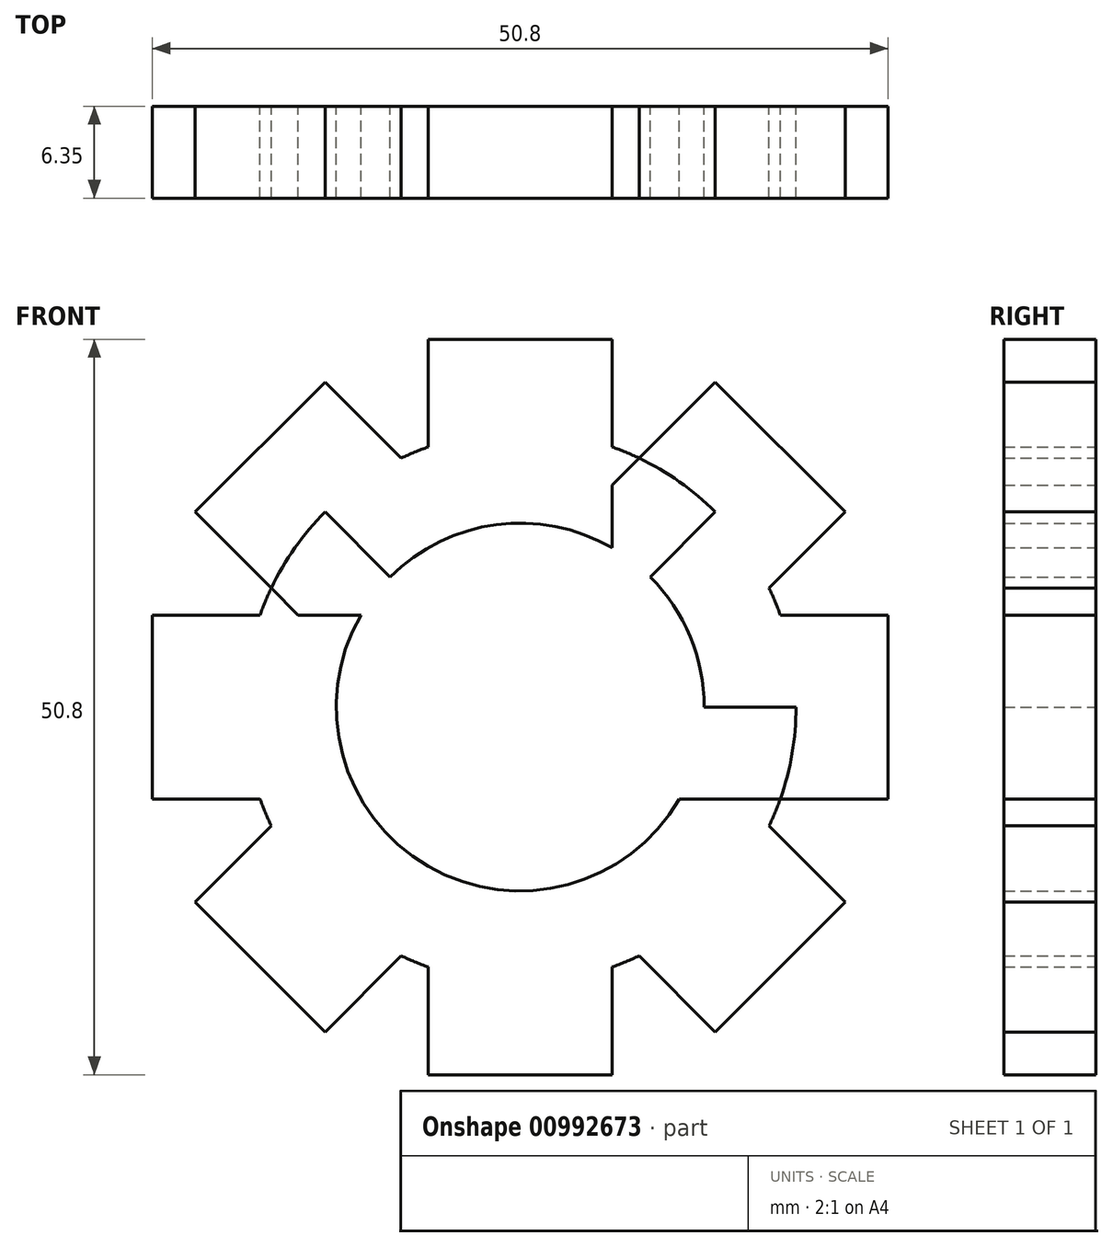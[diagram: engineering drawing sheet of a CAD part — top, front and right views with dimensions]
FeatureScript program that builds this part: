
annotation { "Feature Type Name" : "Feature", "Feature Type Description" : "" }
export const myFeature = defineFeature(function(context is Context, id is Id, definition is map)
    precondition{}
    {
        {
            var Q0;
            Q0=qCreatedBy(makeId("Front.planeOp"),FACE);
            var sketch = newSketch(context, id + "F0", { "sketchPlane" : qUnion([Q0])});
            skCircle(sketch, "E0", {"center": v(0, 0) * mm, "radius": 12.7 * mm});
            skCircle(sketch, "E1", {"center": v(0, 0) * mm, "radius": 19.05 * mm});
            skLineSegment(sketch, "E2", {"start": v(0, 0) * mm, "end": v(0, 25.4) * mm});
            skLineSegment(sketch, "E3", {"start": v(0, 0) * mm, "end": v(25.4, 0) * mm});
            skLineSegment(sketch, "E4", {"start": v(25.4, 0) * mm, "end": v(-25.4, 0) * mm});
            skLineSegment(sketch, "E5", {"start": v(0, 0) * mm, "end": v(-25.4, 25.4) * mm});
            skLineSegment(sketch, "E6", {"start": v(0, 0) * mm, "end": v(26.76, 26.76) * mm});
            skLineSegment(sketch, "E7", {"start": v(0, 25.4) * mm, "end": v(-6.35, 25.4) * mm});
            skLineSegment(sketch, "E8", {"start": v(-6.35, 25.4) * mm, "end": v(-6.35, 0) * mm});
            skLineSegment(sketch, "E9", {"start": v(0, 25.4) * mm, "end": v(6.35, 25.4) * mm});
            skLineSegment(sketch, "E10", {"start": v(6.35, 25.4) * mm, "end": v(6.35, 0) * mm});
            skLineSegment(sketch, "E11", {"start": v(-25.4, 0) * mm, "end": v(-25.4, 6.35) * mm});
            skLineSegment(sketch, "E12", {"start": v(-25.4, 6.35) * mm, "end": v(0, 6.35) * mm});
            skLineSegment(sketch, "E13", {"start": v(25.4, 0) * mm, "end": v(25.4, 6.35) * mm});
            skLineSegment(sketch, "E14", {"start": v(25.4, 6.35) * mm, "end": v(0, 6.35) * mm});
            skLineSegment(sketch, "E15", {"start": v(0, 0) * mm, "end": v(17.96, 17.96) * mm});
            skLineSegment(sketch, "E16", {"start": v(0, 0) * mm, "end": v(-17.96, 17.96) * mm});
            skLineSegment(sketch, "E17", {"start": v(-17.96, 17.96) * mm, "end": v(-13.47, 22.45) * mm});
            skLineSegment(sketch, "E18", {"start": v(-13.47, 22.45) * mm, "end": v(-22.45, 13.47) * mm});
            skLineSegment(sketch, "E19", {"start": v(-22.45, 13.47) * mm, "end": v(-8.98, 0) * mm});
            skLineSegment(sketch, "E20", {"start": v(-13.47, 22.45) * mm, "end": v(2.63, 6.35) * mm});
            skLineSegment(sketch, "E21", {"start": v(17.96, 17.96) * mm, "end": v(22.45, 13.47) * mm});
            skLineSegment(sketch, "E22", {"start": v(22.45, 13.47) * mm, "end": v(13.47, 22.45) * mm});
            skLineSegment(sketch, "E23", {"start": v(13.47, 22.45) * mm, "end": v(3.29, 12.27) * mm});
            skLineSegment(sketch, "E24", {"start": v(22.45, 13.47) * mm, "end": v(14.63, 5.64) * mm});
            skLineSegment(sketch, "E25.MirrorCS", {"start": v(-25.4, 0) * mm, "end": v(-25.4, -6.35) * mm});
            skLineSegment(sketch, "E26.MirrorCS", {"start": v(-25.4, -6.35) * mm, "end": v(0, -6.35) * mm});
            skLineSegment(sketch, "E27.MirrorCS", {"start": v(25.4, 0) * mm, "end": v(25.4, -6.35) * mm});
            skLineSegment(sketch, "E28.MirrorCS", {"start": v(25.4, -6.35) * mm, "end": v(0, -6.35) * mm});
            skLineSegment(sketch, "E29.MirrorCS", {"start": v(17.96, -17.96) * mm, "end": v(22.45, -13.47) * mm});
            skLineSegment(sketch, "E30.MirrorCS", {"start": v(22.45, -13.47) * mm, "end": v(13.47, -22.45) * mm});
            skLineSegment(sketch, "E31.MirrorCS", {"start": v(13.47, -22.45) * mm, "end": v(3.29, -12.27) * mm});
            skLineSegment(sketch, "E32.MirrorCS", {"start": v(22.45, -13.47) * mm, "end": v(14.63, -5.64) * mm});
            skLineSegment(sketch, "E33.MirrorCS", {"start": v(-6.35, -25.4) * mm, "end": v(-6.35, 0) * mm});
            skLineSegment(sketch, "E34.MirrorCS", {"start": v(6.35, -25.4) * mm, "end": v(6.35, 0) * mm});
            skLineSegment(sketch, "E35.MirrorCS", {"start": v(0, -25.4) * mm, "end": v(6.35, -25.4) * mm});
            skLineSegment(sketch, "E36.MirrorCS", {"start": v(0, -25.4) * mm, "end": v(-6.35, -25.4) * mm});
            skLineSegment(sketch, "E37.MirrorCS", {"start": v(-22.45, -13.47) * mm, "end": v(-8.98, 0) * mm});
            skLineSegment(sketch, "E38.MirrorCS", {"start": v(-13.47, -22.45) * mm, "end": v(2.63, -6.35) * mm});
            skLineSegment(sketch, "E39.MirrorCS", {"start": v(-13.47, -22.45) * mm, "end": v(-22.45, -13.47) * mm});
            skSolve(sketch);
        }
        {
            var Q0;
            {var subQ5=sQuery(id+"F0.wireOp",EDGE,"E11");Q0=makeQuery(id+"F0.imprint","IMPRINT",FACE,{"disambiguationData":[TD([[makeQuery(id+"F0.imprint","IMPRINT",EDGE,{"derivedFrom":subQ5}),-1.0]])]});}
            var Q1;
            {var subQ5=sQuery(id+"F0.wireOp",EDGE,"E25.MirrorCS");Q1=makeQuery(id+"F0.imprint","IMPRINT",FACE,{"disambiguationData":[TD([[makeQuery(id+"F0.imprint","IMPRINT",EDGE,{"derivedFrom":subQ5}),1.0]])]});}
            var Q2;
            {var subQ3=sQuery(id+"F0.wireOp",EDGE,"E19");var subQ7=sQuery(id+"F0.wireOp",EDGE,"E0");var subQ9=makeQuery(id+"F0.imprint","INTERSECT",VERTEX,{"derivedFrom":[subQ7,subQ3]});Q2=makeQuery(id+"F0.imprint","IMPRINT",FACE,{"disambiguationData":[TD([[makeQuery(id+"F0.imprint","IMPRINT",EDGE,{"disambiguationData":[TD([[subQ9,-1.0]])],"derivedFrom":subQ7}),-1.0]])]});}
            var Q3;
            {var subQ5=sQuery(id+"F0.wireOp",EDGE,"E4");var subQ6=sQuery(id+"F0.wireOp",EDGE,"E0");var subQ7=makeQuery(id+"F0.imprint","INTERSECT",VERTEX,{"disambiguationData":[OD(1.0)],"derivedFrom":[subQ6,subQ5]});Q3=makeQuery(id+"F0.imprint","IMPRINT",FACE,{"disambiguationData":[TD([[makeQuery(id+"F0.imprint","IMPRINT",EDGE,{"disambiguationData":[TD([[subQ7,-1.0]])],"derivedFrom":subQ6}),-1.0]])]});}
            var Q4;
            {var subQ0=sQuery(id+"F0.wireOp",EDGE,"E19");var subQ1=sQuery(id+"F0.wireOp",EDGE,"E1");var subQ2=makeQuery(id+"F0.imprint","INTERSECT",VERTEX,{"derivedFrom":[subQ1,subQ0]});Q4=makeQuery(id+"F0.imprint","IMPRINT",FACE,{"disambiguationData":[TD([[makeQuery(id+"F0.imprint","IMPRINT",EDGE,{"disambiguationData":[TD([[subQ2,1.0]])],"derivedFrom":subQ1}),-1.0]])]});}
            var Q5;
            {var subQ0=sQuery(id+"F0.wireOp",EDGE,"E20");var subQ1=sQuery(id+"F0.wireOp",EDGE,"E1");var subQ2=makeQuery(id+"F0.imprint","INTERSECT",VERTEX,{"derivedFrom":[subQ1,subQ0]});Q5=makeQuery(id+"F0.imprint","IMPRINT",FACE,{"disambiguationData":[TD([[makeQuery(id+"F0.imprint","IMPRINT",EDGE,{"disambiguationData":[TD([[subQ2,-1.0]])],"derivedFrom":subQ1}),-1.0]])]});}
            var Q6;
            {var subQ1=sQuery(id+"F0.wireOp",EDGE,"E0");var subQ5=sQuery(id+"F0.wireOp",EDGE,"E8");var subQ6=makeQuery(id+"F0.imprint","INTERSECT",VERTEX,{"derivedFrom":[subQ1,subQ5]});Q6=makeQuery(id+"F0.imprint","IMPRINT",FACE,{"disambiguationData":[TD([[makeQuery(id+"F0.imprint","IMPRINT",EDGE,{"disambiguationData":[TD([[subQ6,-1.0]])],"derivedFrom":subQ1}),-1.0]])]});}
            var Q7;
            {var subQ0=sQuery(id+"F0.wireOp",EDGE,"E16");var subQ1=sQuery(id+"F0.wireOp",EDGE,"E0");var subQ2=makeQuery(id+"F0.imprint","INTERSECT",VERTEX,{"derivedFrom":[subQ1,subQ0]});Q7=makeQuery(id+"F0.imprint","IMPRINT",FACE,{"disambiguationData":[TD([[makeQuery(id+"F0.imprint","IMPRINT",EDGE,{"disambiguationData":[TD([[subQ2,-1.0]])],"derivedFrom":subQ1}),-1.0]])]});}
            var Q8;
            {var subQ0=sQuery(id+"F0.wireOp",EDGE,"E2");var subQ1=sQuery(id+"F0.wireOp",EDGE,"E0");var subQ2=makeQuery(id+"F0.imprint","INTERSECT",VERTEX,{"derivedFrom":[subQ1,subQ0]});Q8=makeQuery(id+"F0.imprint","IMPRINT",FACE,{"disambiguationData":[TD([[makeQuery(id+"F0.imprint","IMPRINT",EDGE,{"disambiguationData":[TD([[subQ2,-1.0]])],"derivedFrom":subQ1}),-1.0]])]});}
            var Q9;
            {var subQ5=sQuery(id+"F0.wireOp",EDGE,"E7");Q9=makeQuery(id+"F0.imprint","IMPRINT",FACE,{"disambiguationData":[TD([[makeQuery(id+"F0.imprint","IMPRINT",EDGE,{"derivedFrom":subQ5}),1.0]])]});}
            var Q10;
            {var subQ0=sQuery(id+"F0.wireOp",EDGE,"E20");var subQ1=sQuery(id+"F0.wireOp",EDGE,"E0");var subQ2=makeQuery(id+"F0.imprint","INTERSECT",VERTEX,{"derivedFrom":[subQ1,subQ0]});Q10=makeQuery(id+"F0.imprint","IMPRINT",FACE,{"disambiguationData":[TD([[makeQuery(id+"F0.imprint","IMPRINT",EDGE,{"disambiguationData":[TD([[subQ2,-1.0]])],"derivedFrom":subQ1}),-1.0]])]});}
            var Q11;
            {var subQ5=sQuery(id+"F0.wireOp",EDGE,"E9");Q11=makeQuery(id+"F0.imprint","IMPRINT",FACE,{"disambiguationData":[TD([[makeQuery(id+"F0.imprint","IMPRINT",EDGE,{"derivedFrom":subQ5}),-1.0]])]});}
            var Q12;
            {var subQ0=sQuery(id+"F0.wireOp",EDGE,"E8");var subQ1=sQuery(id+"F0.wireOp",EDGE,"E1");var subQ2=makeQuery(id+"F0.imprint","INTERSECT",VERTEX,{"derivedFrom":[subQ1,subQ0]});Q12=makeQuery(id+"F0.imprint","IMPRINT",FACE,{"disambiguationData":[TD([[makeQuery(id+"F0.imprint","IMPRINT",EDGE,{"disambiguationData":[TD([[subQ2,-1.0]])],"derivedFrom":subQ1}),1.0]])]});}
            var Q13;
            {var subQ0=sQuery(id+"F0.wireOp",EDGE,"E19");var subQ1=sQuery(id+"F0.wireOp",EDGE,"E1");var subQ2=makeQuery(id+"F0.imprint","INTERSECT",VERTEX,{"derivedFrom":[subQ1,subQ0]});Q13=makeQuery(id+"F0.imprint","IMPRINT",FACE,{"disambiguationData":[TD([[makeQuery(id+"F0.imprint","IMPRINT",EDGE,{"disambiguationData":[TD([[subQ2,-1.0]])],"derivedFrom":subQ1}),1.0]])]});}
            var Q14;
            {var subQ1=sQuery(id+"F0.wireOp",EDGE,"E0");var subQ7=sQuery(id+"F0.wireOp",EDGE,"E23");var subQ9=makeQuery(id+"F0.imprint","INTERSECT",VERTEX,{"derivedFrom":[subQ1,subQ7]});Q14=makeQuery(id+"F0.imprint","IMPRINT",FACE,{"disambiguationData":[TD([[makeQuery(id+"F0.imprint","IMPRINT",EDGE,{"disambiguationData":[TD([[subQ9,-1.0]])],"derivedFrom":subQ1}),-1.0]])]});}
            var Q15;
            {var subQ0=sQuery(id+"F0.wireOp",EDGE,"E23");var subQ1=sQuery(id+"F0.wireOp",EDGE,"E1");var subQ2=makeQuery(id+"F0.imprint","INTERSECT",VERTEX,{"derivedFrom":[subQ1,subQ0]});Q15=makeQuery(id+"F0.imprint","IMPRINT",FACE,{"disambiguationData":[TD([[makeQuery(id+"F0.imprint","IMPRINT",EDGE,{"disambiguationData":[TD([[subQ2,-1.0]])],"derivedFrom":subQ1}),1.0]])]});}
            var Q16;
            {var subQ0=sQuery(id+"F0.wireOp",EDGE,"E23");var subQ1=sQuery(id+"F0.wireOp",EDGE,"E0");var subQ2=makeQuery(id+"F0.imprint","INTERSECT",VERTEX,{"derivedFrom":[subQ1,subQ0]});Q16=makeQuery(id+"F0.imprint","IMPRINT",FACE,{"disambiguationData":[TD([[makeQuery(id+"F0.imprint","IMPRINT",EDGE,{"disambiguationData":[TD([[subQ2,1.0]])],"derivedFrom":subQ1}),-1.0]])]});}
            var Q17;
            {var subQ0=sQuery(id+"F0.wireOp",EDGE,"E15");var subQ1=sQuery(id+"F0.wireOp",EDGE,"E0");var subQ2=makeQuery(id+"F0.imprint","INTERSECT",VERTEX,{"derivedFrom":[subQ1,subQ0]});Q17=makeQuery(id+"F0.imprint","IMPRINT",FACE,{"disambiguationData":[TD([[makeQuery(id+"F0.imprint","IMPRINT",EDGE,{"disambiguationData":[TD([[subQ2,-1.0]])],"derivedFrom":subQ1}),-1.0]])]});}
            var Q18;
            {var subQ0=sQuery(id+"F0.wireOp",EDGE,"E23");var subQ1=sQuery(id+"F0.wireOp",EDGE,"E1");var subQ2=makeQuery(id+"F0.imprint","INTERSECT",VERTEX,{"derivedFrom":[subQ1,subQ0]});Q18=makeQuery(id+"F0.imprint","IMPRINT",FACE,{"disambiguationData":[TD([[makeQuery(id+"F0.imprint","IMPRINT",EDGE,{"disambiguationData":[TD([[subQ2,1.0]])],"derivedFrom":subQ1}),-1.0]])]});}
            var Q19;
            {var subQ0=sQuery(id+"F0.wireOp",EDGE,"E24");var subQ1=sQuery(id+"F0.wireOp",EDGE,"E1");var subQ2=makeQuery(id+"F0.imprint","INTERSECT",VERTEX,{"derivedFrom":[subQ1,subQ0]});Q19=makeQuery(id+"F0.imprint","IMPRINT",FACE,{"disambiguationData":[TD([[makeQuery(id+"F0.imprint","IMPRINT",EDGE,{"disambiguationData":[TD([[subQ2,-1.0]])],"derivedFrom":subQ1}),-1.0]])]});}
            var Q20;
            {var subQ1=sQuery(id+"F0.wireOp",EDGE,"E14");var subQ3=sQuery(id+"F0.wireOp",EDGE,"E0");var subQ4=makeQuery(id+"F0.imprint","INTERSECT",VERTEX,{"derivedFrom":[subQ3,subQ1]});Q20=makeQuery(id+"F0.imprint","IMPRINT",FACE,{"disambiguationData":[TD([[makeQuery(id+"F0.imprint","IMPRINT",EDGE,{"disambiguationData":[TD([[subQ4,-1.0]])],"derivedFrom":subQ3}),-1.0]])]});}
            var Q21;
            {var subQ1=sQuery(id+"F0.wireOp",EDGE,"E0");var subQ5=sQuery(id+"F0.wireOp",EDGE,"E14");var subQ8=makeQuery(id+"F0.imprint","INTERSECT",VERTEX,{"derivedFrom":[subQ1,subQ5]});Q21=makeQuery(id+"F0.imprint","IMPRINT",FACE,{"disambiguationData":[TD([[makeQuery(id+"F0.imprint","IMPRINT",EDGE,{"disambiguationData":[TD([[subQ8,1.0]])],"derivedFrom":subQ1}),-1.0]])]});}
            var Q22;
            {var subQ5=sQuery(id+"F0.wireOp",EDGE,"E13");Q22=makeQuery(id+"F0.imprint","IMPRINT",FACE,{"disambiguationData":[TD([[makeQuery(id+"F0.imprint","IMPRINT",EDGE,{"derivedFrom":subQ5}),1.0]])]});}
            var Q23;
            {var subQ0=sQuery(id+"F0.wireOp",EDGE,"E14");var subQ1=sQuery(id+"F0.wireOp",EDGE,"E1");var subQ2=makeQuery(id+"F0.imprint","INTERSECT",VERTEX,{"derivedFrom":[subQ1,subQ0]});Q23=makeQuery(id+"F0.imprint","IMPRINT",FACE,{"disambiguationData":[TD([[makeQuery(id+"F0.imprint","IMPRINT",EDGE,{"disambiguationData":[TD([[subQ2,-1.0]])],"derivedFrom":subQ1}),1.0]])]});}
            var Q24;
            {var subQ5=sQuery(id+"F0.wireOp",EDGE,"E27.MirrorCS");Q24=makeQuery(id+"F0.imprint","IMPRINT",FACE,{"disambiguationData":[TD([[makeQuery(id+"F0.imprint","IMPRINT",EDGE,{"derivedFrom":subQ5}),-1.0]])]});}
            var Q25;
            {var subQ0=sQuery(id+"F0.wireOp",EDGE,"E4");var subQ1=sQuery(id+"F0.wireOp",EDGE,"E0");var subQ2=makeQuery(id+"F0.imprint","INTERSECT",VERTEX,{"disambiguationData":[OD(0.0)],"derivedFrom":[subQ1,subQ0]});Q25=makeQuery(id+"F0.imprint","IMPRINT",FACE,{"disambiguationData":[TD([[makeQuery(id+"F0.imprint","IMPRINT",EDGE,{"disambiguationData":[TD([[subQ2,1.0]])],"derivedFrom":subQ1}),-1.0]])]});}
            var Q26;
            {var subQ3=sQuery(id+"F0.wireOp",EDGE,"E34.MirrorCS");var subQ5=sQuery(id+"F0.wireOp",EDGE,"E0");var subQ6=makeQuery(id+"F0.imprint","INTERSECT",VERTEX,{"derivedFrom":[subQ5,subQ3]});Q26=makeQuery(id+"F0.imprint","IMPRINT",FACE,{"disambiguationData":[TD([[makeQuery(id+"F0.imprint","IMPRINT",EDGE,{"disambiguationData":[TD([[subQ6,-1.0]])],"derivedFrom":subQ5}),-1.0]])]});}
            var Q27;
            {var subQ0=sQuery(id+"F0.wireOp",EDGE,"E31.MirrorCS");var subQ1=sQuery(id+"F0.wireOp",EDGE,"E1");var subQ2=makeQuery(id+"F0.imprint","INTERSECT",VERTEX,{"derivedFrom":[subQ1,subQ0]});Q27=makeQuery(id+"F0.imprint","IMPRINT",FACE,{"disambiguationData":[TD([[makeQuery(id+"F0.imprint","IMPRINT",EDGE,{"disambiguationData":[TD([[subQ2,-1.0]])],"derivedFrom":subQ1}),-1.0]])]});}
            var Q28;
            {var subQ0=sQuery(id+"F0.wireOp",EDGE,"E31.MirrorCS");var subQ1=sQuery(id+"F0.wireOp",EDGE,"E0");var subQ2=makeQuery(id+"F0.imprint","INTERSECT",VERTEX,{"derivedFrom":[subQ1,subQ0]});Q28=makeQuery(id+"F0.imprint","IMPRINT",FACE,{"disambiguationData":[TD([[makeQuery(id+"F0.imprint","IMPRINT",EDGE,{"disambiguationData":[TD([[subQ2,1.0]])],"derivedFrom":subQ1}),-1.0]])]});}
            var Q29;
            {var subQ1=sQuery(id+"F0.wireOp",EDGE,"E0");var subQ8=sQuery(id+"F0.wireOp",EDGE,"E26.MirrorCS");var subQ10=makeQuery(id+"F0.imprint","INTERSECT",VERTEX,{"derivedFrom":[subQ1,subQ8]});Q29=makeQuery(id+"F0.imprint","IMPRINT",FACE,{"disambiguationData":[TD([[makeQuery(id+"F0.imprint","IMPRINT",EDGE,{"disambiguationData":[TD([[subQ10,-1.0]])],"derivedFrom":subQ1}),-1.0]])]});}
            var Q30;
            {var subQ5=sQuery(id+"F0.wireOp",EDGE,"E39.MirrorCS");Q30=makeQuery(id+"F0.imprint","IMPRINT",FACE,{"disambiguationData":[TD([[makeQuery(id+"F0.imprint","IMPRINT",EDGE,{"derivedFrom":subQ5}),-1.0]])]});}
            var Q31;
            {var subQ0=sQuery(id+"F0.wireOp",EDGE,"E35.MirrorCS");Q31=makeQuery(id+"F0.imprint","IMPRINT",FACE,{"disambiguationData":[TD([[makeQuery(id+"F0.imprint","IMPRINT",EDGE,{"derivedFrom":subQ0}),1.0]])]});}
            var Q32;
            {var subQ0=sQuery(id+"F0.wireOp",EDGE,"E31.MirrorCS");var subQ1=sQuery(id+"F0.wireOp",EDGE,"E0");var subQ2=makeQuery(id+"F0.imprint","INTERSECT",VERTEX,{"derivedFrom":[subQ1,subQ0]});Q32=makeQuery(id+"F0.imprint","IMPRINT",FACE,{"disambiguationData":[TD([[makeQuery(id+"F0.imprint","IMPRINT",EDGE,{"disambiguationData":[TD([[subQ2,-1.0]])],"derivedFrom":subQ1}),-1.0]])]});}
            var Q33;
            {var subQ0=sQuery(id+"F0.wireOp",EDGE,"E33.MirrorCS");var subQ1=sQuery(id+"F0.wireOp",EDGE,"E0");var subQ2=makeQuery(id+"F0.imprint","INTERSECT",VERTEX,{"derivedFrom":[subQ1,subQ0]});Q33=makeQuery(id+"F0.imprint","IMPRINT",FACE,{"disambiguationData":[TD([[makeQuery(id+"F0.imprint","IMPRINT",EDGE,{"disambiguationData":[TD([[subQ2,-1.0]])],"derivedFrom":subQ1}),-1.0]])]});}
            var Q34;
            {var subQ0=sQuery(id+"F0.wireOp",EDGE,"E37.MirrorCS");var subQ1=sQuery(id+"F0.wireOp",EDGE,"E0");var subQ2=makeQuery(id+"F0.imprint","INTERSECT",VERTEX,{"derivedFrom":[subQ1,subQ0]});Q34=makeQuery(id+"F0.imprint","IMPRINT",FACE,{"disambiguationData":[TD([[makeQuery(id+"F0.imprint","IMPRINT",EDGE,{"disambiguationData":[TD([[subQ2,-1.0]])],"derivedFrom":subQ1}),-1.0]])]});}
            var Q35;
            {var subQ0=sQuery(id+"F0.wireOp",EDGE,"E12");var subQ1=sQuery(id+"F0.wireOp",EDGE,"E0");var subQ2=makeQuery(id+"F0.imprint","INTERSECT",VERTEX,{"derivedFrom":[subQ1,subQ0]});Q35=makeQuery(id+"F0.imprint","IMPRINT",FACE,{"disambiguationData":[TD([[makeQuery(id+"F0.imprint","IMPRINT",EDGE,{"disambiguationData":[TD([[subQ2,-1.0]])],"derivedFrom":subQ1}),-1.0]])]});}
            var Q36;
            {var subQ0=sQuery(id+"F0.wireOp",EDGE,"E32.MirrorCS");var subQ1=sQuery(id+"F0.wireOp",EDGE,"E1");var subQ2=makeQuery(id+"F0.imprint","INTERSECT",VERTEX,{"derivedFrom":[subQ1,subQ0]});Q36=makeQuery(id+"F0.imprint","IMPRINT",FACE,{"disambiguationData":[TD([[makeQuery(id+"F0.imprint","IMPRINT",EDGE,{"disambiguationData":[TD([[subQ2,-1.0]])],"derivedFrom":subQ1}),1.0]])]});}
            var Q37;
            {var subQ0=sQuery(id+"F0.wireOp",EDGE,"E34.MirrorCS");var subQ1=sQuery(id+"F0.wireOp",EDGE,"E1");var subQ2=makeQuery(id+"F0.imprint","INTERSECT",VERTEX,{"derivedFrom":[subQ1,subQ0]});Q37=makeQuery(id+"F0.imprint","IMPRINT",FACE,{"disambiguationData":[TD([[makeQuery(id+"F0.imprint","IMPRINT",EDGE,{"disambiguationData":[TD([[subQ2,-1.0]])],"derivedFrom":subQ1}),1.0]])]});}
            var Q38;
            {var subQ0=sQuery(id+"F0.wireOp",EDGE,"E38.MirrorCS");var subQ1=sQuery(id+"F0.wireOp",EDGE,"E1");var subQ2=makeQuery(id+"F0.imprint","INTERSECT",VERTEX,{"derivedFrom":[subQ1,subQ0]});Q38=makeQuery(id+"F0.imprint","IMPRINT",FACE,{"disambiguationData":[TD([[makeQuery(id+"F0.imprint","IMPRINT",EDGE,{"disambiguationData":[TD([[subQ2,-1.0]])],"derivedFrom":subQ1}),1.0]])]});}
            var Q39;
            {var subQ0=sQuery(id+"F0.wireOp",EDGE,"E26.MirrorCS");var subQ1=sQuery(id+"F0.wireOp",EDGE,"E1");var subQ2=makeQuery(id+"F0.imprint","INTERSECT",VERTEX,{"derivedFrom":[subQ1,subQ0]});Q39=makeQuery(id+"F0.imprint","IMPRINT",FACE,{"disambiguationData":[TD([[makeQuery(id+"F0.imprint","IMPRINT",EDGE,{"disambiguationData":[TD([[subQ2,-1.0]])],"derivedFrom":subQ1}),1.0]])]});}
            extrude(context, id + "F1", {"entities" : qUnion([Q0, Q1, Q2, Q3, Q4, Q5, Q6, Q7, Q8, Q9, Q10, Q11, Q12, Q13, Q14, Q15, Q16, Q17, Q18, Q19, Q20, Q21, Q22, Q23, Q24, Q25, Q26, Q27, Q28, Q29, Q30, Q31, Q32, Q33, Q34, Q35, Q36, Q37, Q38, Q39]), "depth" : 6.35 * mm, "offsetDistance" : 25.4 * mm});
        }
    });
